# Revit family: 602891Knight WHB 055-399 ATS
name_source: partatom
category: Mechanical Equipment
revit_build: Autodesk Revit 2017 (Build: 20190507_1515(x64)
units: mm (PartAtom-declared; Revit-internal decimal feet)

## family parameters
Cut with Voids When Loaded = No
Host = Face
OmniClass Number = 23.65.35.11
OmniClass Title = Supply Water Heaters
Part Type = Normal
Room Calculation Point = No
Round Connector Dimension = Use Diameter
Shared = Yes

## types (14) — shared parameters
ASME Tank Construction = Yes
Assembly Code = D3020100
Bottom Water Height = 18 7/8"
Default Elevation = 0"
Description = Knight Fire Tube Boiler
Drain Connection Diameter = 3/4"
Frequency = 60 Hz
Manufacturer = Lochinvar
Material = Metal-Lochinvar-Steel
Phase = 1
Price = Prices may vary. Please consult Manufacturer Representative for most up-to-date price list.
Product Documentation Link = http://www.lochinvar.com
Product Page URL = http://www.lochinvar.com
Top Water Height = 18 7/8"
URL = http://www.lochinvar.com
Voltage = 120 V
Warranty Information = 15-Year Limited Warranty, 5-Year Limited Parts Warranty
Water Connection = Yes

## per-type parameters (varying)
- WHB055N: A=40"; Air Intake Connection Description=Air Intake Connection 2"; Air Intake Connection Diameter=2"; B=18 3/4"; Bottom Cold Water Description=Bottom Cold Water Connection Inlet 1'' NPT; Bottom Hot Water Description=Bottom Hot Water Connection Outlet 1'' NPT; C=16"; Cold Water Connection Description=Top Cold Water Connection Inlet 1'' NPT; Cold Water Connection Diameter=1"; D=31 1/8"; E=8 1/2"; Exhaust Air Connection Description=Exhaust Air Connection 2"; Exhaust Air Connection Diameter=2"; F=3 3/4"; Fuel Type=Natural Gas; G=4 1/2"; Gas Connection Description=Gas Supply Connection 1/2"; Gas Supply Connection Diameter=1/2"; H=6 1/2"; Hood Width=40"; Hot Water Connection Description=Top Hot Water Connection Outlet 1'' NPT; Hot Water Connection Diameter=1"; I=7 1/4"; J=8 7/8"; K=3 1/2"; L=1 1/2"; M=1 1/2"; N=6"; Shipping Weight=140 lb; Total Heating Capacity=51000.0 Btu/h; Water Diameter=1"
- WHB085N: A=39 3/4"; Air Intake Connection Description=Air Intake Connection 2"; Air Intake Connection Diameter=2"; B=18 3/4"; Bottom Cold Water Description=Bottom Cold Water Connection Inlet 1'' NPT; Bottom Hot Water Description=Bottom Hot Water Connection Outlet 1'' NPT; C=16"; Cold Water Connection Description=Top Cold Water Connection Inlet 1'' NPT; Cold Water Connection Diameter=1"; D=31 1/8"; E=8 1/2"; Exhaust Air Connection Description=Exhaust Air Connection 2"; Exhaust Air Connection Diameter=2"; F=3 3/4"; Fuel Type=Natural Gas; G=4 1/2"; Gas Connection Description=Gas Supply Connection 1/2"; Gas Supply Connection Diameter=1/2"; H=6 1/2"; Hood Width=39 3/4"; Hot Water Connection Description=Top Hot Water Connection Outlet 1'' NPT; Hot Water Connection Diameter=1"; I=7 1/4"; J=8 7/8"; K=3 1/2"; L=1 1/2"; M=1 1/2"; N=6"; Shipping Weight=140 lb; Total Heating Capacity=79000.0 Btu/h; Water Diameter=1"
- WHB110N: A=41 1/4"; Air Intake Connection Description=Air Intake Connection 3"; Air Intake Connection Diameter=3"; B=18 3/4"; Bottom Cold Water Description=Bottom Cold Water Connection Inlet 1'' NPT; Bottom Hot Water Description=Bottom Hot Water Connection Outlet 1'' NPT; C=19"; Cold Water Connection Description=Top Cold Water Connection Inlet 1'' NPT; Cold Water Connection Diameter=1"; D=31 1/8"; E=10"; Exhaust Air Connection Description=Exhaust Air Connection 3"; Exhaust Air Connection Diameter=3"; F=2 3/4"; Fuel Type=Natural Gas; G=5"; Gas Connection Description=Gas Supply Connection 1/2"; Gas Supply Connection Diameter=1/2"; H=5 1/4"; Hood Width=41 1/4"; Hot Water Connection Description=Top Hot Water Connection Outlet 1'' NPT; Hot Water Connection Diameter=1"; I=11 1/2"; J=8 1/2"; K=5"; L=1"; M=1"; N=4 1/2"; Shipping Weight=160 lb; Total Heating Capacity=102000.0 Btu/h; Water Diameter=1"
- WHB155N: A=41 1/4"; Air Intake Connection Description=Air Intake Connection 3"; Air Intake Connection Diameter=3"; B=18 3/4"; Bottom Cold Water Description=Bottom Cold Water Connection Inlet 1'' NPT; Bottom Hot Water Description=Bottom Hot Water Connection Outlet 1'' NPT; C=19 1/8"; Cold Water Connection Description=Top Cold Water Connection Inlet 1'' NPT; Cold Water Connection Diameter=1"; D=31 1/8"; E=10"; Exhaust Air Connection Description=Exhaust Air Connection 3"; Exhaust Air Connection Diameter=3"; F=2 3/4"; Fuel Type=Natural Gas; G=5"; Gas Connection Description=Gas Supply Connection 1/2"; Gas Supply Connection Diameter=1/2"; H=5 1/4"; Hood Width=41 1/4"; Hot Water Connection Description=Top Hot Water Connection Outlet 1'' NPT; Hot Water Connection Diameter=1"; I=11 1/2"; J=8 1/2"; K=5"; L=1"; M=1"; N=4 1/2"; Shipping Weight=170 lb; Total Heating Capacity=144000.0 Btu/h; Water Diameter=1"
- WHB199N: A=41 1/4"; Air Intake Connection Description=Air Intake Connection 3"; Air Intake Connection Diameter=3"; B=18 3/4"; Bottom Cold Water Description=Bottom Cold Water Connection Inlet 1-1/4'' NPT; Bottom Hot Water Description=Bottom Hot Water Connection Outlet 1-1/4'' NPT; C=19 1/8"; Cold Water Connection Description=Top Cold Water Connection Inlet 1-1/4'' NPT; Cold Water Connection Diameter=1 1/4"; D=31 1/8"; E=10 1/2"; Exhaust Air Connection Description=Exhaust Air Connection 3"; Exhaust Air Connection Diameter=3"; F=3"; Fuel Type=Natural Gas; G=5 1/4"; Gas Connection Description=Gas Supply Connection 1/2"; Gas Supply Connection Diameter=1/2"; H=6"; Hood Width=41 1/4"; Hot Water Connection Description=Top Hot Water Connection Outlet 1-1/4'' NPT; Hot Water Connection Diameter=1"; I=11"; J=9 1/2"; K=6 1/4"; L=1 1/2"; M=1 1/2"; N=4 1/2"; Shipping Weight=180 lb; Total Heating Capacity=184000.0 Btu/h; Water Diameter=1 1/4"
- WHB285N: A=41 3/4"; Air Intake Connection Description=Air Intake Connection 3"; Air Intake Connection Diameter=3"; B=18 3/4"; Bottom Cold Water Description=Bottom Cold Water Connection Inlet 1-1/4'' NPT; Bottom Hot Water Description=Bottom Hot Water Connection Outlet 1-1/4'' NPT; C=21 1/8"; Cold Water Connection Description=Top Cold Water Connection Inlet 1-1/4'' NPT; Cold Water Connection Diameter=1 1/4"; D=31 1/8"; E=15"; Exhaust Air Connection Description=Exhaust Air Connection 3"; Exhaust Air Connection Diameter=3"; F=3"; Fuel Type=Natural Gas; G=3 3/4"; Gas Connection Description=Gas Supply Connection 1/2"; Gas Supply Connection Diameter=1/2"; H=5 1/4"; Hood Width=41 3/4"; Hot Water Connection Description=Top Hot Water Connection Outlet 1-1/4'' NPT; Hot Water Connection Diameter=1"; I=12 1/4"; J=11"; K=6 1/4"; L=1 1/2"; M=1 1/2"; N=6 1/2"; Shipping Weight=180 lb; Total Heating Capacity=264000.0 Btu/h; Water Diameter=1 1/4"
- WHB399N: A=43 5/8"; Air Intake Connection Description=Air Intake Connection 4"; Air Intake Connection Diameter=4"; B=25 1/4"; Bottom Cold Water Description=Bottom Cold Water Connection Inlet 1-1/2'' NPT; Bottom Hot Water Description=Bottom Hot Water Connection Outlet 1-1/2'' NPT; C=21 7/8"; Cold Water Connection Description=Top Cold Water Connection Inlet 1-1/2'' NPT; Cold Water Connection Diameter=1 1/2"; D=34 3/8"; E=3 1/8"; Exhaust Air Connection Description=Exhaust Air Connection 4"; Exhaust Air Connection Diameter=4"; F=4 1/4"; Fuel Type=Natural Gas; G=23"; Gas Connection Description=Gas Supply Connection 3/4"; Gas Supply Connection Diameter=3/4"; H=3 7/8"; Hood Width=43 5/8"; Hot Water Connection Description=Top Hot Water Connection Outlet 1-1/2'' NPT; Hot Water Connection Diameter=2"; I=8 3/4"; J=12 1/2"; K=9 1/4"; L=2"; M=2"; N=23"; Shipping Weight=210 lb; Total Heating Capacity=377000.0 Btu/h; Water Diameter=1 1/2"
- WHB055L: A=40"; Air Intake Connection Description=Air Intake Connection 2"; Air Intake Connection Diameter=2"; B=18 3/4"; Bottom Cold Water Description=Bottom Cold Water Connection Inlet 1'' NPT; Bottom Hot Water Description=Bottom Hot Water Connection Outlet 1'' NPT; C=16"; Cold Water Connection Description=Top Cold Water Connection Inlet 1'' NPT; Cold Water Connection Diameter=1"; D=31 1/8"; E=8 1/2"; Exhaust Air Connection Description=Exhaust Air Connection 2"; Exhaust Air Connection Diameter=2"; F=3 3/4"; Fuel Type=LP Gas; G=4 1/2"; Gas Connection Description=Gas Supply Connection 1/2"; Gas Supply Connection Diameter=1/2"; H=6 1/2"; Hood Width=40"; Hot Water Connection Description=Top Hot Water Connection Outlet 1'' NPT; Hot Water Connection Diameter=1"; I=7 1/4"; J=8 7/8"; K=3 1/2"; L=1 1/2"; M=1 1/2"; N=6"; Shipping Weight=140 lb; Total Heating Capacity=51000.0 Btu/h; Water Diameter=1"
- WHB085L: A=39 3/4"; Air Intake Connection Description=Air Intake Connection 2"; Air Intake Connection Diameter=2"; B=18 3/4"; Bottom Cold Water Description=Bottom Cold Water Connection Inlet 1'' NPT; Bottom Hot Water Description=Bottom Hot Water Connection Outlet 1'' NPT; C=16"; Cold Water Connection Description=Top Cold Water Connection Inlet 1'' NPT; Cold Water Connection Diameter=1"; D=31 1/8"; E=8 1/2"; Exhaust Air Connection Description=Exhaust Air Connection 2"; Exhaust Air Connection Diameter=2"; F=3 3/4"; Fuel Type=LP Gas; G=4 1/2"; Gas Connection Description=Gas Supply Connection 1/2"; Gas Supply Connection Diameter=1/2"; H=6 1/2"; Hood Width=39 3/4"; Hot Water Connection Description=Top Hot Water Connection Outlet 1'' NPT; Hot Water Connection Diameter=1"; I=7 1/4"; J=8 7/8"; K=3 1/2"; L=1 1/2"; M=1 1/2"; N=6"; Shipping Weight=140 lb; Total Heating Capacity=79000.0 Btu/h; Water Diameter=1"
- WHB110L: A=41 1/4"; Air Intake Connection Description=Air Intake Connection 3"; Air Intake Connection Diameter=3"; B=18 3/4"; Bottom Cold Water Description=Bottom Cold Water Connection Inlet 1'' NPT; Bottom Hot Water Description=Bottom Hot Water Connection Outlet 1'' NPT; C=19"; Cold Water Connection Description=Top Cold Water Connection Inlet 1'' NPT; Cold Water Connection Diameter=1"; D=31 1/8"; E=10"; Exhaust Air Connection Description=Exhaust Air Connection 3"; Exhaust Air Connection Diameter=3"; F=2 3/4"; Fuel Type=LP Gas; G=5"; Gas Connection Description=Gas Supply Connection 1/2"; Gas Supply Connection Diameter=1/2"; H=5 1/4"; Hood Width=41 1/4"; Hot Water Connection Description=Top Hot Water Connection Outlet 1'' NPT; Hot Water Connection Diameter=1"; I=11 1/2"; J=8 1/2"; K=5"; L=1"; M=1"; N=4 1/2"; Shipping Weight=160 lb; Total Heating Capacity=102000.0 Btu/h; Water Diameter=1"
- WHB155L: A=41 1/4"; Air Intake Connection Description=Air Intake Connection 3"; Air Intake Connection Diameter=3"; B=18 3/4"; Bottom Cold Water Description=Bottom Cold Water Connection Inlet 1'' NPT; Bottom Hot Water Description=Bottom Hot Water Connection Outlet 1'' NPT; C=19 1/8"; Cold Water Connection Description=Top Cold Water Connection Inlet 1'' NPT; Cold Water Connection Diameter=1"; D=31 1/8"; E=10"; Exhaust Air Connection Description=Exhaust Air Connection 3"; Exhaust Air Connection Diameter=3"; F=2 3/4"; Fuel Type=LP Gas; G=5"; Gas Connection Description=Gas Supply Connection 1/2"; Gas Supply Connection Diameter=1/2"; H=5 1/4"; Hood Width=41 1/4"; Hot Water Connection Description=Top Hot Water Connection Outlet 1'' NPT; Hot Water Connection Diameter=1"; I=11 1/2"; J=8 1/2"; K=5"; L=1"; M=1"; N=4 1/2"; Shipping Weight=170 lb; Total Heating Capacity=144000.0 Btu/h; Water Diameter=1"
- WHB199L: A=41 1/4"; Air Intake Connection Description=Air Intake Connection 3"; Air Intake Connection Diameter=3"; B=18 3/4"; Bottom Cold Water Description=Bottom Cold Water Connection Inlet 1-1/4'' NPT; Bottom Hot Water Description=Bottom Hot Water Connection Outlet 1-1/4'' NPT; C=19 1/8"; Cold Water Connection Description=Top Cold Water Connection Inlet 1-1/4'' NPT; Cold Water Connection Diameter=1 1/4"; D=31 1/8"; E=10 1/2"; Exhaust Air Connection Description=Exhaust Air Connection 3"; Exhaust Air Connection Diameter=3"; F=3"; Fuel Type=LP Gas; G=5 1/4"; Gas Connection Description=Gas Supply Connection 1/2"; Gas Supply Connection Diameter=1/2"; H=6"; Hood Width=41 1/4"; Hot Water Connection Description=Top Hot Water Connection Outlet 1-1/4'' NPT; Hot Water Connection Diameter=1"; I=11"; J=9 1/2"; K=6 1/4"; L=1 1/2"; M=1 1/2"; N=4 1/2"; Shipping Weight=180 lb; Total Heating Capacity=184000.0 Btu/h; Water Diameter=1 1/4"
- WHB285L: A=41 3/4"; Air Intake Connection Description=Air Intake Connection 3"; Air Intake Connection Diameter=3"; B=18 3/4"; Bottom Cold Water Description=Bottom Cold Water Connection Inlet 1-1/4'' NPT; Bottom Hot Water Description=Bottom Hot Water Connection Outlet 1-1/4'' NPT; C=21 1/8"; Cold Water Connection Description=Top Cold Water Connection Inlet 1-1/4'' NPT; Cold Water Connection Diameter=1 1/4"; D=31 1/8"; E=15"; Exhaust Air Connection Description=Exhaust Air Connection 3"; Exhaust Air Connection Diameter=3"; F=3"; Fuel Type=LP Gas; G=3 3/4"; Gas Connection Description=Gas Supply Connection 1/2"; Gas Supply Connection Diameter=1/2"; H=5 1/4"; Hood Width=41 3/4"; Hot Water Connection Description=Top Hot Water Connection Outlet 1-1/4'' NPT; Hot Water Connection Diameter=1"; I=12 1/4"; J=11"; K=6 1/4"; L=1 1/2"; M=1 1/2"; N=6 1/2"; Shipping Weight=180 lb; Total Heating Capacity=264000.0 Btu/h; Water Diameter=1 1/4"
- WHB399L: A=43 5/8"; Air Intake Connection Description=Air Intake Connection 4"; Air Intake Connection Diameter=4"; B=25 1/4"; Bottom Cold Water Description=Bottom Cold Water Connection Inlet 1-1/2'' NPT; Bottom Hot Water Description=Bottom Hot Water Connection Outlet 1-1/2'' NPT; C=21 7/8"; Cold Water Connection Description=Top Cold Water Connection Inlet 1-1/2'' NPT; Cold Water Connection Diameter=1 1/2"; D=34 3/8"; E=3 1/8"; Exhaust Air Connection Description=Exhaust Air Connection 4"; Exhaust Air Connection Diameter=4"; F=4 1/4"; Fuel Type=LP Gas; G=23"; Gas Connection Description=Gas Supply Connection 3/4"; Gas Supply Connection Diameter=3/4"; H=3 7/8"; Hood Width=43 5/8"; Hot Water Connection Description=Top Hot Water Connection Outlet 1-1/2'' NPT; Hot Water Connection Diameter=2"; I=8 3/4"; J=12 1/2"; K=9 1/4"; L=2"; M=2"; N=23"; Shipping Weight=210 lb; Total Heating Capacity=377000.0 Btu/h; Water Diameter=1 1/2"

note: column(s) folded — value = type name in every type: Model

## geometry (parser evidence)
native form markers: Sweep x4
no freeform markers — native parametric forms only
